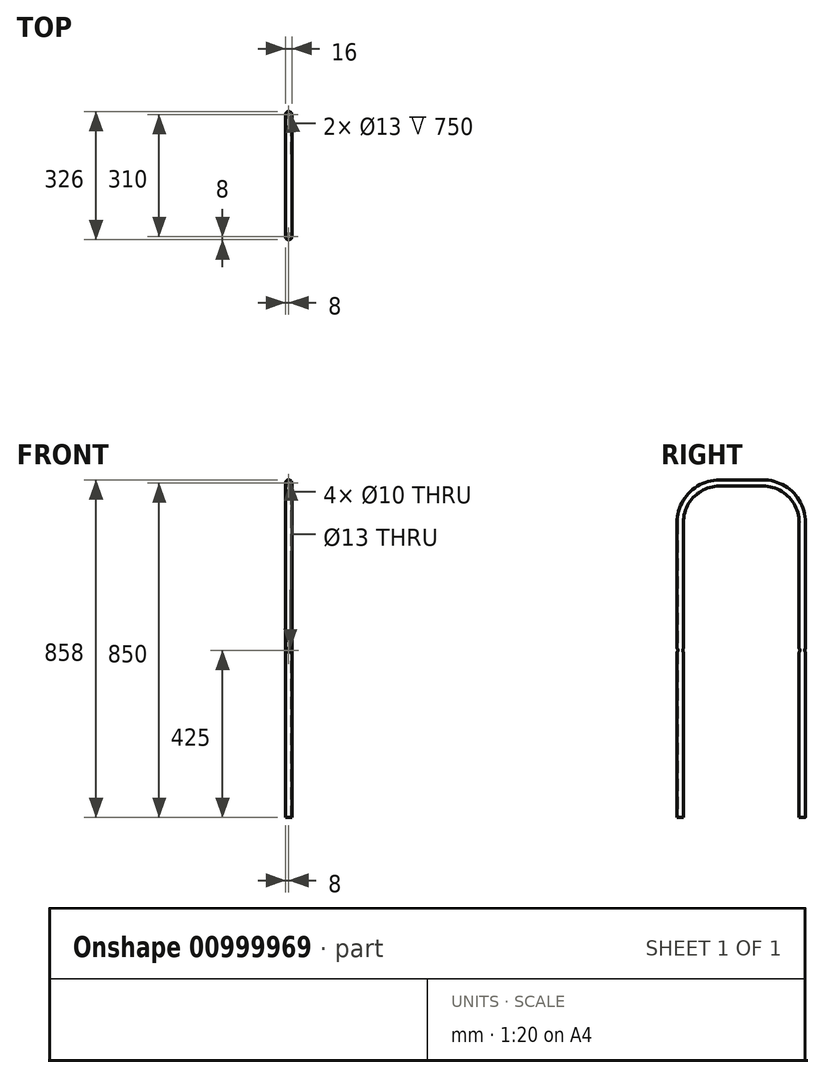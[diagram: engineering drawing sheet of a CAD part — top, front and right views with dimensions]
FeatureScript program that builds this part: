
annotation { "Feature Type Name" : "Feature", "Feature Type Description" : "" }
export const myFeature = defineFeature(function(context is Context, id is Id, definition is map)
    precondition{}
    {
        {
            var Q0;
            Q0=qCreatedBy(makeId("Right.planeOp"),FACE);
            var sketch = newSketch(context, id + "F0", { "sketchPlane" : qUnion([Q0])});
            skLineSegment(sketch, "E0.top", {"start": v(-100, 850) * mm, "end": v(-210, 850) * mm});
            skLineSegment(sketch, "E0.left", {"start": v(0, 0) * mm, "end": v(0, 750) * mm});
            skLineSegment(sketch, "E0.right", {"start": v(-310, 0) * mm, "end": v(-310, 750) * mm});
            skPoint(sketch, "E1.visualSharp", {"position": v(-310, 850) * mm});
            skArc(sketch, "E1.filletArc", {"start": v(-210, 850) * mm, "mid": v(-280.71, 820.71) * mm, "end": v(-310, 750) * mm});
            skPoint(sketch, "E2.visualSharp", {"position": v(0, 850) * mm});
            skArc(sketch, "E2.filletArc", {"start": v(0, 750) * mm, "mid": v(-29.29, 820.71) * mm, "end": v(-100, 850) * mm});
            skSolve(sketch);
        }
        {
            var Q0;
            Q0=qCreatedBy(makeId("Top.planeOp"),FACE);
            var sketch = newSketch(context, id + "F1", { "sketchPlane" : qUnion([Q0])});
            skCircle(sketch, "E3", {"center": v(0, 0) * mm, "radius": 8 * mm});
            skSolve(sketch);
        }
        {
            var Q0;
            Q0=makeQuery(id+"F1.imprint","IMPRINT",FACE,{"disambiguationData":[TD([[makeQuery(id+"F1.imprint","IMPRINT",EDGE,{"derivedFrom":sQuery(id+"F1.wireOp",EDGE,"E3")}),1.0]])]});
            var Q1;
            Q1=sQuery(id+"F0.wireOp",EDGE,"E0.right");
            var Q2;
            Q2=sQuery(id+"F0.wireOp",EDGE,"E0.top");
            var Q3;
            Q3=sQuery(id+"F0.wireOp",EDGE,"E1.filletArc");
            var Q4;
            Q4=sQuery(id+"F0.wireOp",EDGE,"E2.filletArc");
            var Q5;
            Q5=sQuery(id+"F0.wireOp",EDGE,"E0.left");
            sweep(context, id + "F2", {"profiles" : qUnion([Q0]), "path" : qUnion([Q1, Q2, Q3, Q4, Q5])});
        }
        {
            var Q0;
            Q0=makeQuery(id+"F2.opSweep","CAP_FACE",FACE,{"disambiguationData":[OSD([sQuery(id+"F0.wireOp",VERTEX,"E0.right.start"),sQuery(id+"F1.wireOp",EDGE,"E3")])],"isStart":false});
            var Q1;
            Q1=makeQuery(id+"F2.opSweep","CAP_FACE",FACE,{"disambiguationData":[OSD([sQuery(id+"F0.wireOp",VERTEX,"E0.left.start"),sQuery(id+"F1.wireOp",EDGE,"E3")])],"isStart":true});
            shell(context, id + "F3", {"entities" : qUnion([Q0, Q1]), "thickness" : 1.5 * mm});
        }
        {
            var Q0;
            Q0=qCreatedBy(makeId("Front.planeOp"),FACE);
            var sketch = newSketch(context, id + "F4", { "sketchPlane" : qUnion([Q0])});
            skLineSegment(sketch, "E4", {"start": v(0, 425) * mm, "end": v(25.62, 425) * mm});
            skSolve(sketch);
        }
        {
            var Q0;
            Q0=sQuery(id+"F4.wireOp",VERTEX,"E4.start");
            var Q1;
            Q1=makeQuery(id+"F2.opSweep","SWEPT_BODY",BODY,{"disambiguationData":[OSD([sQuery(id+"F0.wireOp",EDGE,"E0.left"),sQuery(id+"F1.wireOp",EDGE,"E3")])]});
            hole(context, id + "F5", {"style" : HoleStyle.SIMPLE, "endStyle" : HoleEndStyle.THROUGH, "oppositeDirection" : true, "holeDiameter" : 10 * mm, "majorDiameter" : 5 * mm, "isTappedThrough" : true, "tappedDepth" : 12 * mm, "tapClearance" : 3, "locations" : qUnion([Q0]), "scope" : qUnion([Q1])});
        }
        {
            var Q0;
            Q0=sQuery(id+"F4.wireOp",VERTEX,"E4.start");
            var Q1;
            Q1=makeQuery(id+"F2.opSweep","SWEPT_BODY",BODY,{"disambiguationData":[OSD([sQuery(id+"F0.wireOp",EDGE,"E0.left"),sQuery(id+"F1.wireOp",EDGE,"E3")])]});
            hole(context, id + "F6", {"style" : HoleStyle.SIMPLE, "endStyle" : HoleEndStyle.THROUGH, "holeDiameter" : 10 * mm, "majorDiameter" : 5 * mm, "isTappedThrough" : true, "tappedDepth" : 12 * mm, "tapClearance" : 3, "locations" : qUnion([Q0]), "scope" : qUnion([Q1])});
        }
    });
